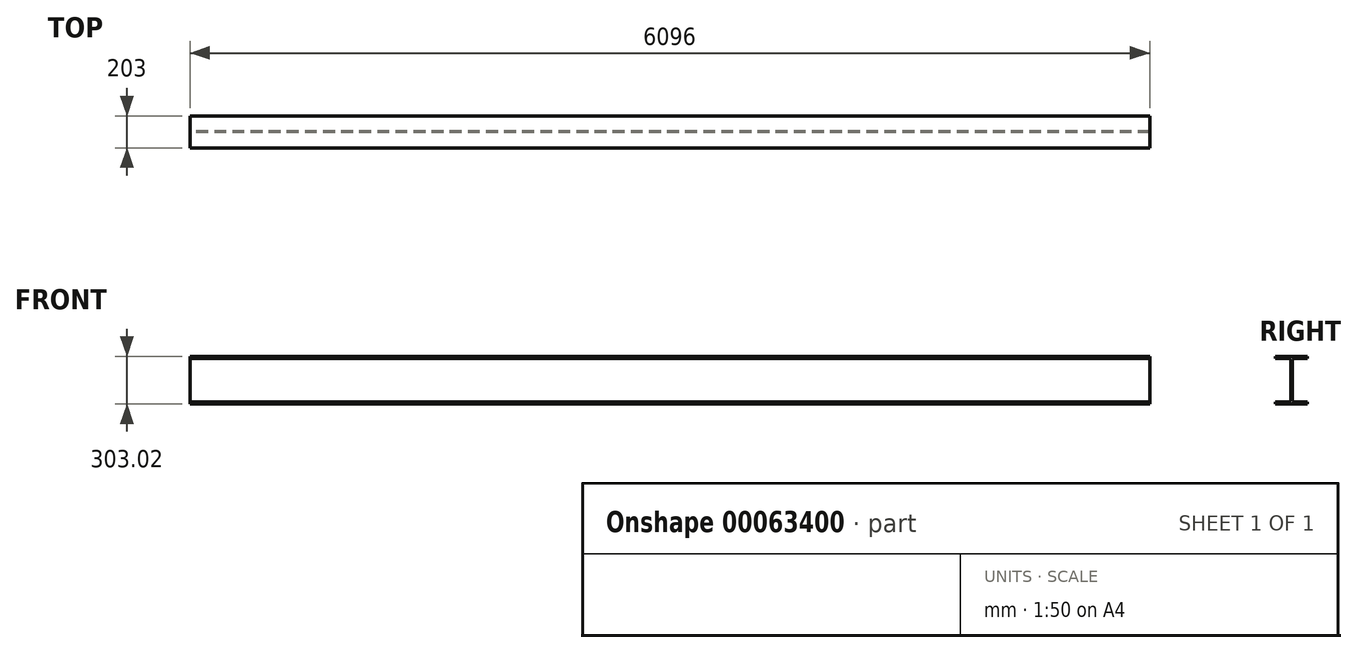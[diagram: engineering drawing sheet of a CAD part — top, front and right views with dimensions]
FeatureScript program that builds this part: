
annotation { "Feature Type Name" : "Feature", "Feature Type Description" : "" }
export const myFeature = defineFeature(function(context is Context, id is Id, definition is map)
    precondition{}
    {
        {
            var Q0;
            Q0=qCreatedBy(makeId("Right.planeOp"),FACE);
            var sketch = newSketch(context, id + "F0", { "sketchPlane" : qUnion([Q0])});
            skLineSegment(sketch, "E0", {"start": v(-3.75, 0) * mm, "end": v(-3.75, 118.52) * mm});
            skLineSegment(sketch, "E1", {"start": v(-23.64, 138.41) * mm, "end": v(-101.5, 138.41) * mm});
            skLineSegment(sketch, "E2", {"start": v(-101.5, 138.41) * mm, "end": v(-101.5, 151.51) * mm});
            skLineSegment(sketch, "E3", {"start": v(-101.5, 151.51) * mm, "end": v(0, 151.51) * mm});
            skLineSegment(sketch, "E4.MirrorCS", {"start": v(101.5, 138.41) * mm, "end": v(101.5, 151.51) * mm});
            skLineSegment(sketch, "E5.MirrorCS", {"start": v(23.64, 138.41) * mm, "end": v(101.5, 138.41) * mm});
            skLineSegment(sketch, "E6.MirrorCS", {"start": v(3.75, 0) * mm, "end": v(3.75, 118.52) * mm});
            skLineSegment(sketch, "E7.MirrorCS", {"start": v(101.5, 151.51) * mm, "end": v(0, 151.51) * mm});
            skLineSegment(sketch, "E8.MirrorCS", {"start": v(101.5, -151.51) * mm, "end": v(0, -151.51) * mm});
            skLineSegment(sketch, "E9.MirrorCS", {"start": v(3.75, 0) * mm, "end": v(3.75, -118.52) * mm});
            skLineSegment(sketch, "E10.MirrorCS", {"start": v(-23.64, -138.41) * mm, "end": v(-101.5, -138.41) * mm});
            skLineSegment(sketch, "E11.MirrorCS", {"start": v(101.5, -138.41) * mm, "end": v(101.5, -151.51) * mm});
            skLineSegment(sketch, "E12.MirrorCS", {"start": v(-3.75, 0) * mm, "end": v(-3.75, -118.52) * mm});
            skLineSegment(sketch, "E13.MirrorCS", {"start": v(23.64, -138.41) * mm, "end": v(101.5, -138.41) * mm});
            skLineSegment(sketch, "E14.MirrorCS", {"start": v(-101.5, -138.41) * mm, "end": v(-101.5, -151.51) * mm});
            skLineSegment(sketch, "E15.MirrorCS", {"start": v(-101.5, -151.51) * mm, "end": v(0, -151.51) * mm});
            skPoint(sketch, "E16.visualSharp", {"position": v(-3.75, 138.41) * mm});
            skArc(sketch, "E16.filletArc", {"start": v(-3.75, 118.52) * mm, "mid": v(-9.57, 132.59) * mm, "end": v(-23.64, 138.41) * mm});
            skPoint(sketch, "E17.visualSharp", {"position": v(3.75, 138.41) * mm});
            skArc(sketch, "E17.filletArc", {"start": v(23.64, 138.41) * mm, "mid": v(9.57, 132.59) * mm, "end": v(3.75, 118.52) * mm});
            skPoint(sketch, "E18.visualSharp", {"position": v(3.75, -138.41) * mm});
            skArc(sketch, "E18.filletArc", {"start": v(3.75, -118.52) * mm, "mid": v(9.57, -132.59) * mm, "end": v(23.64, -138.41) * mm});
            skPoint(sketch, "E19.visualSharp", {"position": v(-3.75, -138.41) * mm});
            skArc(sketch, "E19.filletArc", {"start": v(-23.64, -138.41) * mm, "mid": v(-9.57, -132.59) * mm, "end": v(-3.75, -118.52) * mm});
            skSolve(sketch);
        }
        {
            var Q0;
            Q0=makeQuery(id+"F0.imprint","IMPRINT",FACE,{"disambiguationData":[TD([[makeQuery(id+"F0.imprint","IMPRINT",EDGE,{"derivedFrom":sQuery(id+"F0.wireOp",EDGE,"E0")}),-1.0]])]});
            extrude(context, id + "F1", {"entities" : qUnion([Q0]), "depth" : 6096 * mm});
        }
        {
            var Q0;
            Q0=makeQuery(id+"F1.opExtrude","CAP_FACE",FACE,{"disambiguationData":[OSD([sQuery(id+"F0.wireOp",EDGE,"E0"),sQuery(id+"F0.wireOp",EDGE,"E1"),sQuery(id+"F0.wireOp",EDGE,"E2"),sQuery(id+"F0.wireOp",EDGE,"E3"),sQuery(id+"F0.wireOp",EDGE,"E4.MirrorCS"),sQuery(id+"F0.wireOp",EDGE,"E5.MirrorCS"),sQuery(id+"F0.wireOp",EDGE,"E6.MirrorCS"),sQuery(id+"F0.wireOp",EDGE,"E7.MirrorCS"),sQuery(id+"F0.wireOp",EDGE,"E8.MirrorCS"),sQuery(id+"F0.wireOp",EDGE,"E9.MirrorCS"),sQuery(id+"F0.wireOp",EDGE,"E10.MirrorCS"),sQuery(id+"F0.wireOp",EDGE,"E11.MirrorCS"),sQuery(id+"F0.wireOp",EDGE,"E12.MirrorCS"),sQuery(id+"F0.wireOp",EDGE,"E13.MirrorCS"),sQuery(id+"F0.wireOp",EDGE,"E14.MirrorCS"),sQuery(id+"F0.wireOp",EDGE,"E15.MirrorCS"),sQuery(id+"F0.wireOp",EDGE,"E16.filletArc"),sQuery(id+"F0.wireOp",EDGE,"E17.filletArc"),sQuery(id+"F0.wireOp",EDGE,"E18.filletArc"),sQuery(id+"F0.wireOp",EDGE,"E19.filletArc")])],"isStart":true});
            cPlane(context, id + "F2", {"entities" : qUnion([Q0]), "cplaneType" : CPlaneType.OFFSET, "offset" : 457.2 * mm, "width" : 152.4 * mm, "height" : 152.4 * mm});
        }
    });
